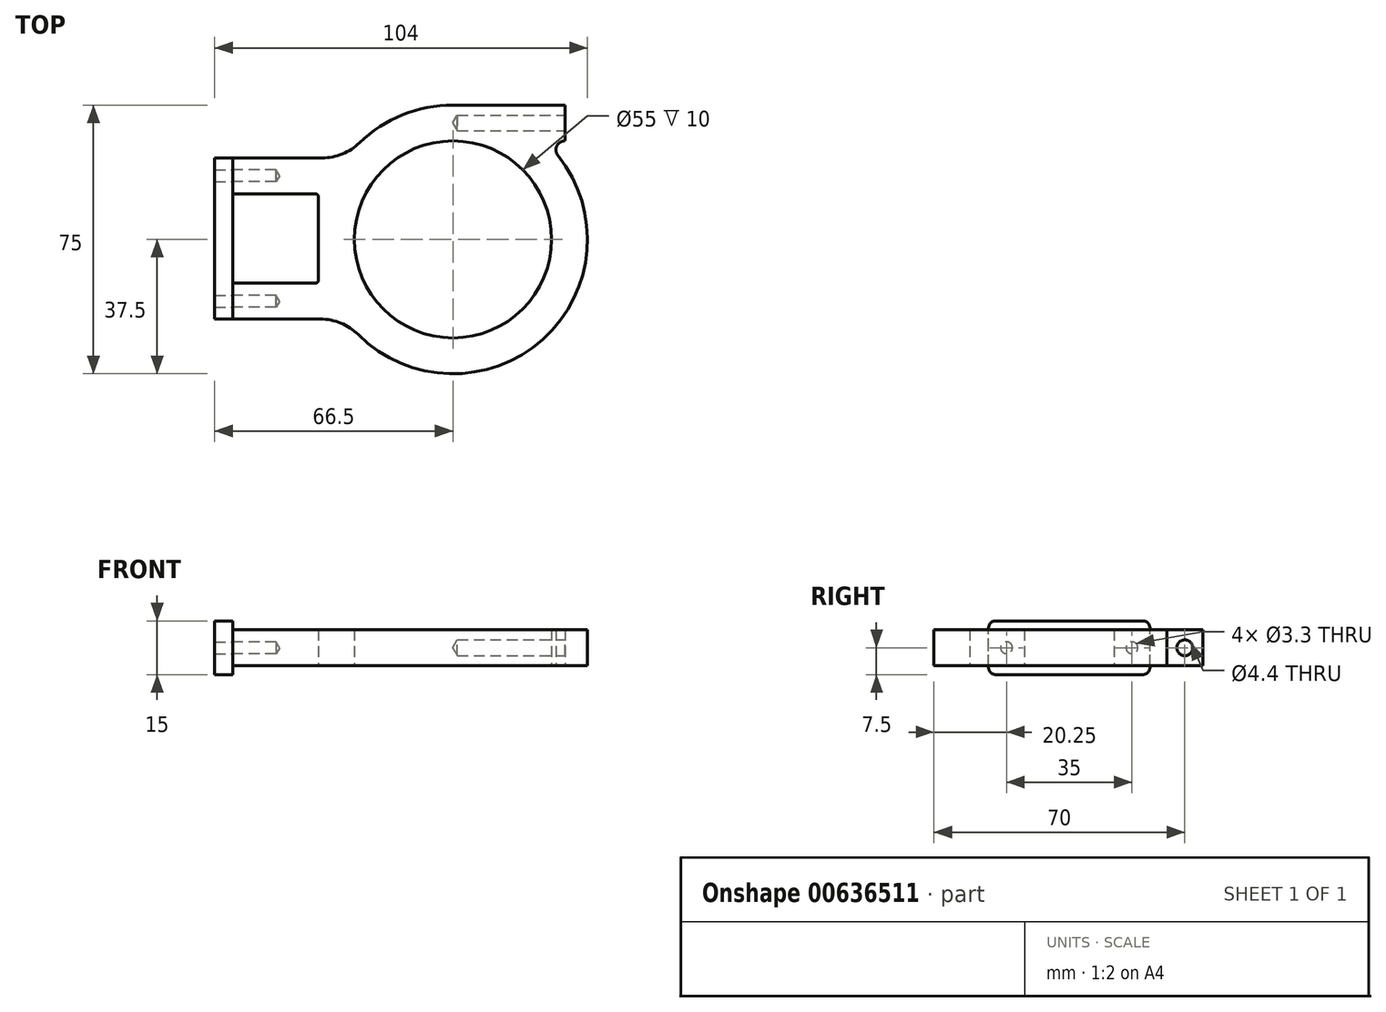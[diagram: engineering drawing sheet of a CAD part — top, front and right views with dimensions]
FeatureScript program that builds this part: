
annotation { "Feature Type Name" : "Feature", "Feature Type Description" : "" }
export const myFeature = defineFeature(function(context is Context, id is Id, definition is map)
    precondition{}
    {
        {
            var Q0;
            Q0=qCreatedBy(makeId("Top.planeOp"),FACE);
            var sketch = newSketch(context, id + "F0", { "sketchPlane" : qUnion([Q0])});
            skLineSegment(sketch, "E0.bottom", {"start": v(-5, 12.75) * mm, "end": v(-29, 12.75) * mm});
            skLineSegment(sketch, "E0.top", {"start": v(-5, -12.25) * mm, "end": v(-29, -12.25) * mm});
            skLineSegment(sketch, "E0.left", {"start": v(-5, 12.75) * mm, "end": v(-5, -12.25) * mm});
            skArc(sketch, "E1", {"start": v(32.5, 27.5) * mm, "mid": v(31, -27.46) * mm, "end": v(35.5, 27.34) * mm});
            skArc(sketch, "E2", {"start": v(6.07, -26.6) * mm, "mid": v(57.56, -27.9) * mm, "end": v(61.77, 23.44) * mm});
            skLineSegment(sketch, "E3.bottom", {"start": v(-29, -22.25) * mm, "end": v(-4.5, -22.25) * mm});
            skLineSegment(sketch, "E3.top", {"start": v(-29, 22.75) * mm, "end": v(-3.99, 22.75) * mm});
            skPoint(sketch, "E4.visualSharp", {"position": v(2.69, 22.75) * mm});
            skArc(sketch, "E4.filletArc", {"start": v(-3.99, 22.75) * mm, "mid": v(1.64, 23.84) * mm, "end": v(6.44, 26.96) * mm});
            skPoint(sketch, "E5.visualSharp", {"position": v(2.31, -22.25) * mm});
            skArc(sketch, "E5.filletArc", {"start": v(6.07, -26.6) * mm, "mid": v(1.22, -23.38) * mm, "end": v(-4.5, -22.25) * mm});
            skLineSegment(sketch, "E6", {"start": v(63.72, 37.5) * mm, "end": v(32.5, 37.5) * mm});
            skArc(sketch, "E7.trimOffspring", {"start": v(32.5, 37.5) * mm, "mid": v(18.44, 34.77) * mm, "end": v(6.44, 26.96) * mm});
            skPoint(sketch, "E8.visualSharp", {"position": v(58, 27.5) * mm});
            skArc(sketch, "E8.filletArc", {"start": v(63.72, 27.5) * mm, "mid": v(61.47, 26.08) * mm, "end": v(61.77, 23.44) * mm});
            skLineSegment(sketch, "E9", {"start": v(63.72, 27.5) * mm, "end": v(63.72, 37.5) * mm});
            skLineSegment(sketch, "E10", {"start": v(-29, 22.75) * mm, "end": v(-29, 12.75) * mm});
            skLineSegment(sketch, "E11.trimOffspring", {"start": v(-29, -12.25) * mm, "end": v(-29, -22.25) * mm});
            skLineSegment(sketch, "E12", {"start": v(63.72, 27.5) * mm, "end": v(100.2, 27.5) * mm, "construction": true});
            skCircle(sketch, "E13", {"center": v(32.5, 0) * mm, "radius": 27.5 * mm});
            skSolve(sketch);
        }
        {
            var Q0;
            Q0=makeQuery(id+"F0.imprint","IMPRINT",FACE,{"disambiguationData":[TD([[makeQuery(id+"F0.imprint","IMPRINT",EDGE,{"derivedFrom":sQuery(id+"F0.wireOp",EDGE,"E0.bottom")}),-1.0]])]});
            extrude(context, id + "F1", {"entities" : qUnion([Q0]), "depth" : 10 * mm, "offsetDistance" : 25 * mm});
        }
        {
            var Q0;
            Q0=makeQuery(id+"F1.opExtrude","SWEPT_FACE",FACE,{"disambiguationData":[OSD([sQuery(id+"F0.wireOp",EDGE,"E9")])]});
            var sketch = newSketch(context, id + "F2", { "sketchPlane" : qUnion([Q0])});
            skPoint(sketch, "E14", {"position": v(32.5, 5) * mm});
            skPoint(sketch, "E14.positionSnap0", {"position": v(32.5, 10) * mm});
            skPoint(sketch, "E14.positionSnap1", {"position": v(37.5, 5) * mm});
            skSolve(sketch);
        }
        {
            var Q0;
            Q0=makeQuery(id+"F1.opExtrude","SWEPT_FACE",FACE,{"disambiguationData":[OSD([sQuery(id+"F0.wireOp",EDGE,"E10")])]});
            var sketch = newSketch(context, id + "F3", { "sketchPlane" : qUnion([Q0])});
            skPoint(sketch, "E15", {"position": v(-17.75, 5) * mm});
            skPoint(sketch, "E15.positionSnap0", {"position": v(-22.75, 5) * mm});
            skPoint(sketch, "E15.positionSnap1", {"position": v(-17.75, 0) * mm});
            skSolve(sketch);
        }
        {
            var Q0;
            Q0=makeQuery(id+"F1.opExtrude","SWEPT_FACE",FACE,{"disambiguationData":[OSD([sQuery(id+"F0.wireOp",EDGE,"E11.trimOffspring")])]});
            var sketch = newSketch(context, id + "F4", { "sketchPlane" : qUnion([Q0])});
            skPoint(sketch, "E16", {"position": v(17.25, 5) * mm});
            skPoint(sketch, "E16.positionSnap0", {"position": v(12.25, 5) * mm});
            skPoint(sketch, "E16.positionSnap1", {"position": v(17.25, 0) * mm});
            skSolve(sketch);
        }
        {
            var Q0;
            Q0=sQuery(id+"F3.wireOp",VERTEX,"E15");
            var Q1;
            Q1=sQuery(id+"F4.wireOp",VERTEX,"E16");
            var Q2;
            Q2=makeQuery(id+"F1.opExtrude","SWEPT_BODY",BODY,{"disambiguationData":[OSD([sQuery(id+"F0.wireOp",EDGE,"E0.bottom"),sQuery(id+"F0.wireOp",EDGE,"E0.top"),sQuery(id+"F0.wireOp",EDGE,"E0.left"),sQuery(id+"F0.wireOp",EDGE,"E1"),sQuery(id+"F0.wireOp",EDGE,"E2"),sQuery(id+"F0.wireOp",EDGE,"E3.bottom"),sQuery(id+"F0.wireOp",EDGE,"E3.top"),sQuery(id+"F0.wireOp",EDGE,"E4.filletArc"),sQuery(id+"F0.wireOp",EDGE,"E5.filletArc"),sQuery(id+"F0.wireOp",EDGE,"nfuTfoKm-p6nO-uxgr-8oEE-wzeqzSAJRhSV"),sQuery(id+"F0.wireOp",EDGE,"E6"),sQuery(id+"F0.wireOp",EDGE,"E7.trimOffspring"),sQuery(id+"F0.wireOp",EDGE,"E8.filletArc"),sQuery(id+"F0.wireOp",EDGE,"E9"),sQuery(id+"F0.wireOp",EDGE,"p3WC6bMz-r61b-FSj3-OULK-L3u69mPWSSPh"),sQuery(id+"F0.wireOp",EDGE,"E10"),sQuery(id+"F0.wireOp",EDGE,"E11.trimOffspring")])]});
            hole(context, id + "F5", {"style" : HoleStyle.SIMPLE, "endStyle" : HoleEndStyle.BLIND, "standardTappedOrClearance" : lookupTablePath({ "standard" : "ISO", "engagement" : "75%", "pitch" : "0.7 mm", "size" : "M4", "type" : "Tapped" }), "standardBlindInLast" : lookupTablePath({ "standard" : "ISO", "engagement" : "75%", "pitch" : "0.7 mm", "size" : "M4", "type" : "Tapped" }), "holeDiameter" : 3.3 * mm, "majorDiameter" : 4 * mm, "showTappedDepth" : true, "holeDepth" : 12.1 * mm, "tappedDepth" : 10 * mm, "tapClearance" : 3, "locations" : qUnion([Q0, Q1]), "scope" : qUnion([Q2])});
        }
        {
            var Q0;
            Q0=sQuery(id+"F2.wireOp",VERTEX,"E14");
            var Q1;
            Q1=makeQuery(id+"F1.opExtrude","SWEPT_BODY",BODY,{"disambiguationData":[OSD([sQuery(id+"F0.wireOp",EDGE,"E0.bottom"),sQuery(id+"F0.wireOp",EDGE,"E0.top"),sQuery(id+"F0.wireOp",EDGE,"E0.left"),sQuery(id+"F0.wireOp",EDGE,"E1"),sQuery(id+"F0.wireOp",EDGE,"E2"),sQuery(id+"F0.wireOp",EDGE,"E3.bottom"),sQuery(id+"F0.wireOp",EDGE,"E3.top"),sQuery(id+"F0.wireOp",EDGE,"E4.filletArc"),sQuery(id+"F0.wireOp",EDGE,"E5.filletArc"),sQuery(id+"F0.wireOp",EDGE,"nfuTfoKm-p6nO-uxgr-8oEE-wzeqzSAJRhSV"),sQuery(id+"F0.wireOp",EDGE,"E6"),sQuery(id+"F0.wireOp",EDGE,"E7.trimOffspring"),sQuery(id+"F0.wireOp",EDGE,"E8.filletArc"),sQuery(id+"F0.wireOp",EDGE,"E9"),sQuery(id+"F0.wireOp",EDGE,"p3WC6bMz-r61b-FSj3-OULK-L3u69mPWSSPh"),sQuery(id+"F0.wireOp",EDGE,"E10"),sQuery(id+"F0.wireOp",EDGE,"E11.trimOffspring")])]});
            hole(context, id + "F6", {"style" : HoleStyle.SIMPLE, "endStyle" : HoleEndStyle.BLIND, "standardTappedOrClearance" : lookupTablePath({ "standard" : "ISO", "fit" : "Normal", "size" : "M4", "type" : "Clearance" }), "standardBlindInLast" : lookupTablePath({ "fit" : "Standard", "standard" : "ISO", "size" : "M4", "type" : "Clearance" }), "holeDiameter" : 4.4 * mm, "majorDiameter" : 4 * mm, "holeDepth" : 30 * mm, "tappedDepth" : 10 * mm, "tapClearance" : 3, "locations" : qUnion([Q0]), "scope" : qUnion([Q1])});
        }
        {
            var Q0;
            Q0=makeQuery(id+"F1.opExtrude","SWEPT_FACE",FACE,{"disambiguationData":[OSD([sQuery(id+"F0.wireOp",EDGE,"E11.trimOffspring")])]});
            var sketch = newSketch(context, id + "F7", { "sketchPlane" : qUnion([Q0])});
            skLineSegment(sketch, "E17.bottom", {"start": v(-22.75, -2.5) * mm, "end": v(22.25, -2.5) * mm});
            skLineSegment(sketch, "E17.top", {"start": v(-22.75, 12.5) * mm, "end": v(22.25, 12.5) * mm});
            skLineSegment(sketch, "E17.left", {"start": v(-22.75, -2.5) * mm, "end": v(-22.75, 12.5) * mm});
            skLineSegment(sketch, "E17.right", {"start": v(22.25, -2.5) * mm, "end": v(22.25, 12.5) * mm});
            skCircle(sketch, "E18.0", {"center": v(-17.75, 5) * mm, "radius": 1.65 * mm});
            skCircle(sketch, "E19.0", {"center": v(17.25, 5) * mm, "radius": 1.65 * mm});
            skSolve(sketch);
        }
        {
            var Q0;
            {var subQ3=sQuery(id+"F7.wireOp",EDGE,"E17.bottom");Q0=makeQuery(id+"F7.imprint","IMPRINT",FACE,{"disambiguationData":[TD([[makeQuery(id+"F7.imprint","IMPRINT",EDGE,{"derivedFrom":subQ3}),1.0]])]});}
            var Q1;
            {var subQ0=sQuery(id+"F0.wireOp",EDGE,"E11.trimOffspring");var subQ2=makeQuery(id+"F1.opExtrude","CAP_EDGE",EDGE,{"disambiguationData":[OSD([subQ0])],"isStart":true});Q1=makeQuery(id+"F7.imprint","IMPRINT",FACE,{"disambiguationData":[TD([[makeQuery(id+"F7.imprint","IMPRINT",EDGE,{"derivedFrom":subQ2}),1.0]])]});}
            extrude(context, id + "F8", {"entities" : qUnion([Q0, Q1]), "depth" : 5 * mm, "offsetDistance" : 25 * mm});
        }
        {
            var Q0;
            Q0=makeQuery(id+"F8.opExtrude","SWEPT_EDGE",EDGE,{"disambiguationData":[OSD([sQuery(id+"F7.wireOp",EDGE,"E17.top"),sQuery(id+"F7.wireOp",EDGE,"E17.left")])]});
            var Q1;
            Q1=makeQuery(id+"F8.opExtrude","SWEPT_EDGE",EDGE,{"disambiguationData":[OSD([sQuery(id+"F7.wireOp",EDGE,"E17.top"),sQuery(id+"F7.wireOp",EDGE,"E17.right")])]});
            var Q2;
            Q2=makeQuery(id+"F8.opExtrude","SWEPT_EDGE",EDGE,{"disambiguationData":[OSD([sQuery(id+"F7.wireOp",EDGE,"E17.bottom"),sQuery(id+"F7.wireOp",EDGE,"E17.right")])]});
            var Q3;
            Q3=makeQuery(id+"F8.opExtrude","SWEPT_EDGE",EDGE,{"disambiguationData":[OSD([sQuery(id+"F7.wireOp",EDGE,"E17.bottom"),sQuery(id+"F7.wireOp",EDGE,"E17.left")])]});
            fillet(context, id + "F9", {"entities" : qUnion([Q0, Q1, Q2, Q3]), "radius" : 2 * mm, "tangentPropagation" : true, "allowEdgeOverflow" : false});
        }
        {
            var Q0;
            Q0=makeQuery(id+"F1.opExtrude","SWEPT_EDGE",EDGE,{"disambiguationData":[OSD([sQuery(id+"F0.wireOp",EDGE,"E0.bottom"),sQuery(id+"F0.wireOp",EDGE,"E0.left")])]});
            var Q1;
            Q1=makeQuery(id+"F1.opExtrude","SWEPT_EDGE",EDGE,{"disambiguationData":[OSD([sQuery(id+"F0.wireOp",EDGE,"E0.top"),sQuery(id+"F0.wireOp",EDGE,"E0.left")])]});
            fillet(context, id + "F10", {"entities" : qUnion([Q0, Q1]), "radius" : 1 * mm, "tangentPropagation" : true, "allowEdgeOverflow" : false});
        }
    });
